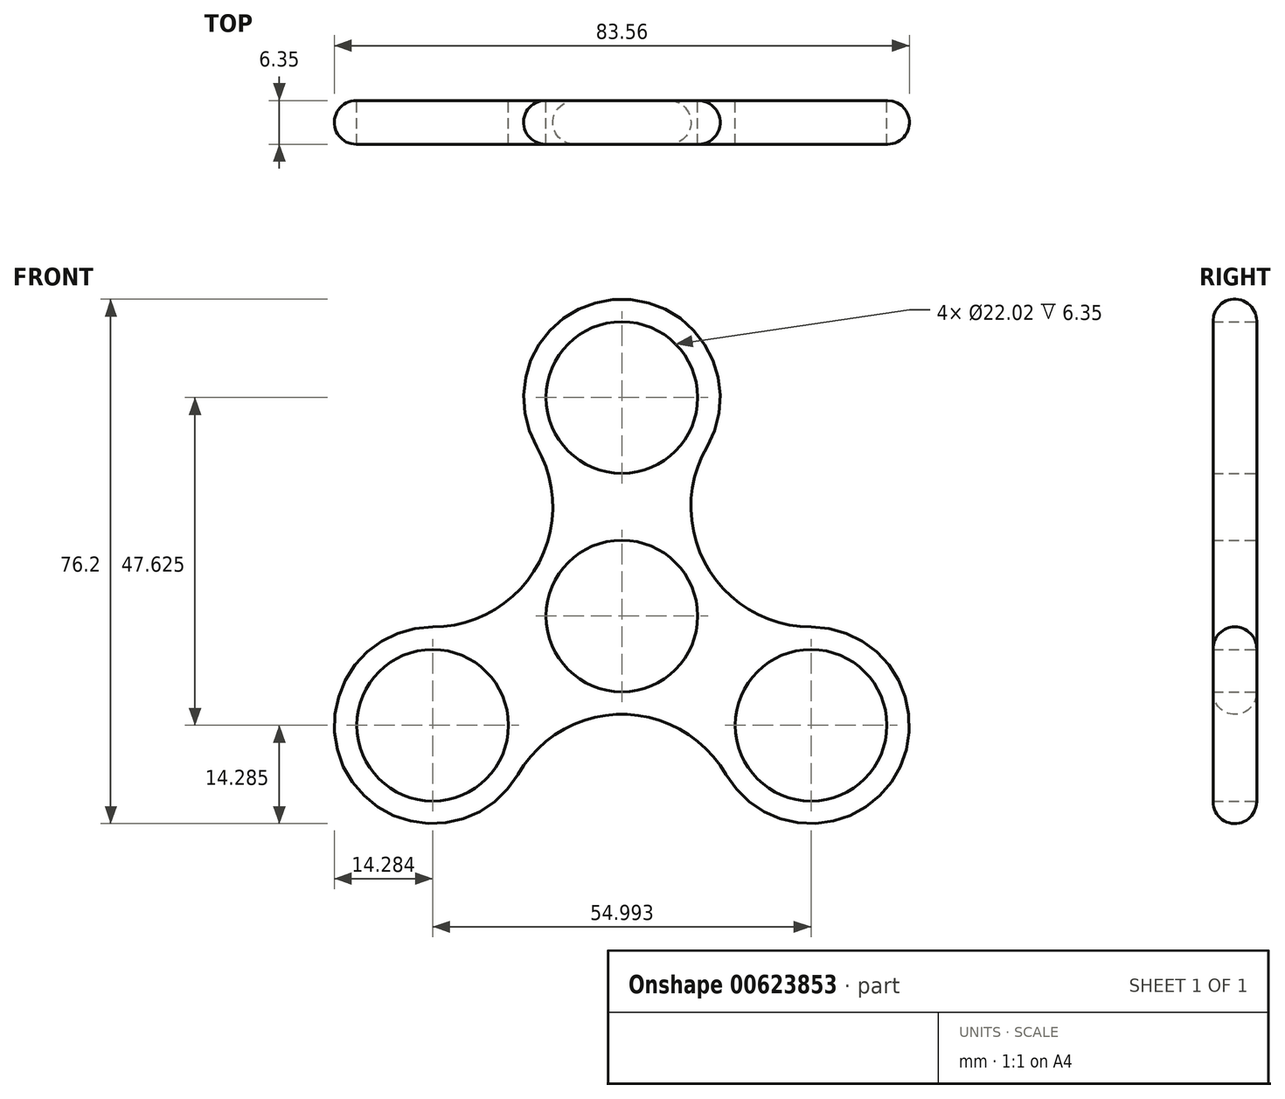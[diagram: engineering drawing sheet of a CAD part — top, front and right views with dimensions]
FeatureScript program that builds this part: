
annotation { "Feature Type Name" : "Feature", "Feature Type Description" : "" }
export const myFeature = defineFeature(function(context is Context, id is Id, definition is map)
    precondition{}
    {
        {
            var Q0;
            Q0=qCreatedBy(makeId("Front.planeOp"),FACE);
            var sketch = newSketch(context, id + "F0", { "sketchPlane" : qUnion([Q0])});
            skCircle(sketch, "E0", {"center": v(0, 31.75) * mm, "radius": 14.29 * mm});
            skCircle(sketch, "E1", {"center": v(0, 31.75) * mm, "radius": 11.01 * mm});
            skCircle(sketch, "E2", {"center": v(0, 0) * mm, "radius": 14.29 * mm});
            skCircle(sketch, "E3", {"center": v(0, 0) * mm, "radius": 11.01 * mm});
            skCircle(sketch, "E4.1.0", {"center": v(-27.5, -15.87) * mm, "radius": 11.01 * mm});
            skCircle(sketch, "E4.1.1", {"center": v(-27.5, -15.87) * mm, "radius": 14.29 * mm});
            skCircle(sketch, "E4.2.0", {"center": v(27.5, -15.88) * mm, "radius": 11.01 * mm});
            skCircle(sketch, "E4.2.1", {"center": v(27.5, -15.88) * mm, "radius": 14.29 * mm});
            skArc(sketch, "E5", {"start": v(15.12, -23.02) * mm, "mid": v(0, -14.29) * mm, "end": v(-15.12, -23.02) * mm});
            skArc(sketch, "E6.1.0", {"start": v(12.37, 24.6) * mm, "mid": v(12.37, 7.14) * mm, "end": v(27.5, -1.59) * mm});
            skArc(sketch, "E6.2.0", {"start": v(-27.5, -1.59) * mm, "mid": v(-12.37, 7.14) * mm, "end": v(-12.37, 24.6) * mm});
            skSolve(sketch);
        }
        {
            var Q0;
            Q0 = qSketchRegion(id + "F0", true);
            extrude(context, id + "F1", {"entities" : qUnion([Q0]), "depth" : 6.35 * mm, "offsetDistance" : 25.4 * mm});
        }
        {
            var Q0;
            Q0=makeQuery(id+"F1.opExtrude","CAP_EDGE",EDGE,{"disambiguationData":[OSD([sQuery(id+"F0.wireOp",EDGE,"E6.2.0")])],"isStart":true});
            var Q1;
            Q1=makeQuery(id+"F1.opExtrude","CAP_EDGE",EDGE,{"disambiguationData":[OSD([sQuery(id+"F0.wireOp",EDGE,"E5")])],"isStart":false});
            fillet(context, id + "F2", {"entities" : qUnion([Q0, Q1]), "radius" : 3.17 * mm, "tangentPropagation" : true, "allowEdgeOverflow" : false});
        }
    });
